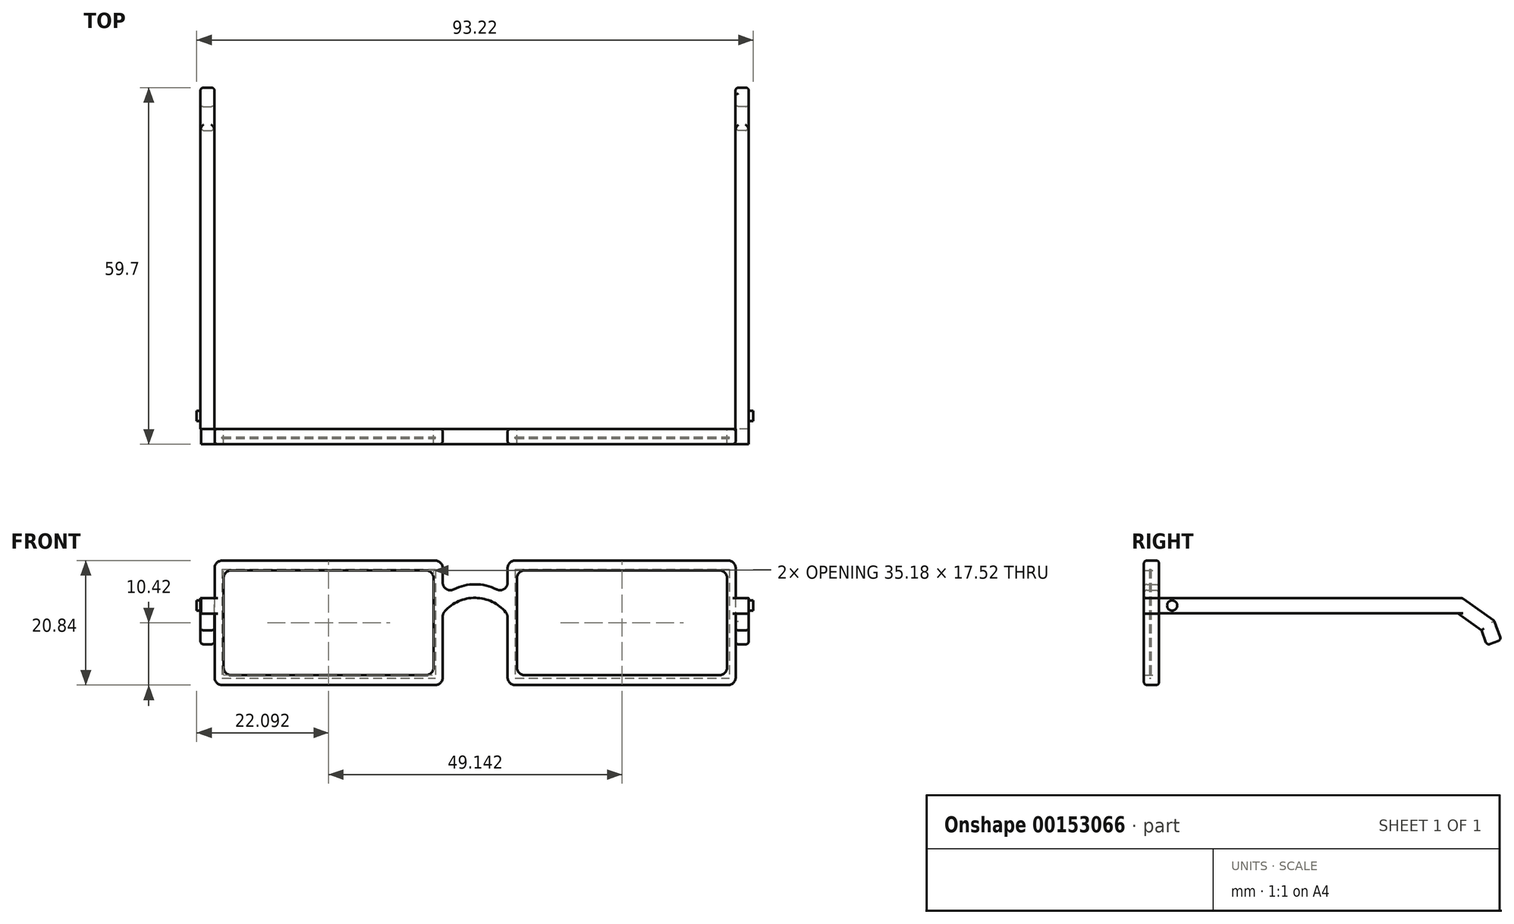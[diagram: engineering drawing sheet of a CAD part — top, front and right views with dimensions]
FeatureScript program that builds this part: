
annotation { "Feature Type Name" : "Feature", "Feature Type Description" : "" }
export const myFeature = defineFeature(function(context is Context, id is Id, definition is map)
    precondition{}
    {
        {
            var Q0;
            Q0=qCreatedBy(makeId("Front.planeOp"),FACE);
            var sketch = newSketch(context, id + "F0", { "sketchPlane" : qUnion([Q0])});
            skLineSegment(sketch, "E0", {"start": v(-49.06, 20.84) * mm, "end": v(-49.06, 0) * mm});
            skLineSegment(sketch, "E1", {"start": v(-49.06, 0) * mm, "end": v(-10.85, 0) * mm});
            skLineSegment(sketch, "E2", {"start": v(-10.85, 20.84) * mm, "end": v(-49.06, 20.84) * mm});
            skArc(sketch, "E3", {"start": v(0, 14.74) * mm, "mid": v(-5.43, 16.86) * mm, "end": v(-10.85, 14.74) * mm});
            skLineSegment(sketch, "E4", {"start": v(-10.85, 20.84) * mm, "end": v(-10.85, 14.74) * mm});
            skArc(sketch, "E5", {"start": v(0, 11.78) * mm, "mid": v(-5.39, 14.6) * mm, "end": v(-10.85, 11.94) * mm});
            skLineSegment(sketch, "E6", {"start": v(-10.85, 11.94) * mm, "end": v(-10.85, 0) * mm});
            skLineSegment(sketch, "E7", {"start": v(0, 14.74) * mm, "end": v(0, 20.84) * mm});
            skLineSegment(sketch, "E8", {"start": v(0, 11.78) * mm, "end": v(0, 0) * mm});
            skLineSegment(sketch, "E9", {"start": v(0, 0) * mm, "end": v(38.2, 0) * mm});
            skLineSegment(sketch, "E10", {"start": v(38.2, 0) * mm, "end": v(38.2, 20.84) * mm});
            skLineSegment(sketch, "E11", {"start": v(38.2, 20.84) * mm, "end": v(0, 20.84) * mm});
            skLineSegment(sketch, "E12.bottom", {"start": v(-47.57, 19.18) * mm, "end": v(-12.39, 19.18) * mm});
            skLineSegment(sketch, "E12.top", {"start": v(-47.57, 1.66) * mm, "end": v(-12.39, 1.66) * mm});
            skLineSegment(sketch, "E12.left", {"start": v(-47.57, 19.18) * mm, "end": v(-47.57, 1.66) * mm});
            skLineSegment(sketch, "E12.right", {"start": v(-12.39, 19.18) * mm, "end": v(-12.39, 1.66) * mm});
            skLineSegment(sketch, "E13.bottom", {"start": v(1.58, 19.18) * mm, "end": v(36.75, 19.18) * mm});
            skLineSegment(sketch, "E13.top", {"start": v(1.58, 1.66) * mm, "end": v(36.75, 1.66) * mm});
            skLineSegment(sketch, "E13.left", {"start": v(1.58, 19.18) * mm, "end": v(1.58, 1.66) * mm});
            skLineSegment(sketch, "E13.right", {"start": v(36.75, 19.18) * mm, "end": v(36.75, 1.66) * mm});
            skSolve(sketch);
        }
        {
            var Q0;
            Q0 = qSketchRegion(id + "F0", true);
            extrude(context, id + "F1", {"entities" : qUnion([Q0]), "depth" : 2.54 * mm});
        }
        {
            var Q0;
            Q0=makeQuery(id+"F1.opExtrude","SWEPT_EDGE",EDGE,{"disambiguationData":[OSD([sQuery(id+"F0.wireOp",EDGE,"E0"),sQuery(id+"F0.wireOp",EDGE,"E2")])]});
            var Q1;
            Q1=makeQuery(id+"F1.opExtrude","SWEPT_EDGE",EDGE,{"disambiguationData":[OSD([sQuery(id+"F0.wireOp",EDGE,"E0"),sQuery(id+"F0.wireOp",EDGE,"E1")])]});
            var Q2;
            Q2=makeQuery(id+"F1.opExtrude","SWEPT_EDGE",EDGE,{"disambiguationData":[OSD([sQuery(id+"F0.wireOp",EDGE,"E2"),sQuery(id+"F0.wireOp",EDGE,"E4")])]});
            var Q3;
            Q3=makeQuery(id+"F1.opExtrude","SWEPT_EDGE",EDGE,{"disambiguationData":[OSD([sQuery(id+"F0.wireOp",EDGE,"E1"),sQuery(id+"F0.wireOp",EDGE,"E6")])]});
            var Q4;
            Q4=makeQuery(id+"F1.opExtrude","SWEPT_EDGE",EDGE,{"disambiguationData":[OSD([sQuery(id+"F0.wireOp",EDGE,"E12.bottom"),sQuery(id+"F0.wireOp",EDGE,"E12.right")])]});
            var Q5;
            Q5=makeQuery(id+"F1.opExtrude","SWEPT_EDGE",EDGE,{"disambiguationData":[OSD([sQuery(id+"F0.wireOp",EDGE,"E12.top"),sQuery(id+"F0.wireOp",EDGE,"E12.right")])]});
            var Q6;
            Q6=makeQuery(id+"F1.opExtrude","SWEPT_EDGE",EDGE,{"disambiguationData":[OSD([sQuery(id+"F0.wireOp",EDGE,"E12.top"),sQuery(id+"F0.wireOp",EDGE,"E12.left")])]});
            var Q7;
            Q7=makeQuery(id+"F1.opExtrude","SWEPT_EDGE",EDGE,{"disambiguationData":[OSD([sQuery(id+"F0.wireOp",EDGE,"E12.bottom"),sQuery(id+"F0.wireOp",EDGE,"E12.left")])]});
            var Q8;
            Q8=makeQuery(id+"F1.opExtrude","SWEPT_EDGE",EDGE,{"disambiguationData":[OSD([sQuery(id+"F0.wireOp",EDGE,"E5"),sQuery(id+"F0.wireOp",EDGE,"E8")])]});
            var Q9;
            Q9=makeQuery(id+"F1.opExtrude","SWEPT_EDGE",EDGE,{"disambiguationData":[OSD([sQuery(id+"F0.wireOp",EDGE,"E5"),sQuery(id+"F0.wireOp",EDGE,"E6")])]});
            var Q10;
            Q10=makeQuery(id+"F1.opExtrude","SWEPT_EDGE",EDGE,{"disambiguationData":[OSD([sQuery(id+"F0.wireOp",EDGE,"E3"),sQuery(id+"F0.wireOp",EDGE,"E4")])]});
            var Q11;
            Q11=makeQuery(id+"F1.opExtrude","SWEPT_EDGE",EDGE,{"disambiguationData":[OSD([sQuery(id+"F0.wireOp",EDGE,"E3"),sQuery(id+"F0.wireOp",EDGE,"E7")])]});
            var Q12;
            Q12=makeQuery(id+"F1.opExtrude","SWEPT_EDGE",EDGE,{"disambiguationData":[OSD([sQuery(id+"F0.wireOp",EDGE,"E7"),sQuery(id+"F0.wireOp",EDGE,"E11")])]});
            var Q13;
            Q13=makeQuery(id+"F1.opExtrude","SWEPT_EDGE",EDGE,{"disambiguationData":[OSD([sQuery(id+"F0.wireOp",EDGE,"E8"),sQuery(id+"F0.wireOp",EDGE,"E9")])]});
            var Q14;
            Q14=makeQuery(id+"F1.opExtrude","SWEPT_EDGE",EDGE,{"disambiguationData":[OSD([sQuery(id+"F0.wireOp",EDGE,"E9"),sQuery(id+"F0.wireOp",EDGE,"E10")])]});
            var Q15;
            Q15=makeQuery(id+"F1.opExtrude","SWEPT_EDGE",EDGE,{"disambiguationData":[OSD([sQuery(id+"F0.wireOp",EDGE,"E10"),sQuery(id+"F0.wireOp",EDGE,"E11")])]});
            var Q16;
            Q16=makeQuery(id+"F1.opExtrude","SWEPT_EDGE",EDGE,{"disambiguationData":[OSD([sQuery(id+"F0.wireOp",EDGE,"E13.top"),sQuery(id+"F0.wireOp",EDGE,"E13.left")])]});
            var Q17;
            Q17=makeQuery(id+"F1.opExtrude","SWEPT_EDGE",EDGE,{"disambiguationData":[OSD([sQuery(id+"F0.wireOp",EDGE,"E13.bottom"),sQuery(id+"F0.wireOp",EDGE,"E13.left")])]});
            var Q18;
            Q18=makeQuery(id+"F1.opExtrude","SWEPT_EDGE",EDGE,{"disambiguationData":[OSD([sQuery(id+"F0.wireOp",EDGE,"E13.bottom"),sQuery(id+"F0.wireOp",EDGE,"E13.right")])]});
            var Q19;
            Q19=makeQuery(id+"F1.opExtrude","SWEPT_EDGE",EDGE,{"disambiguationData":[OSD([sQuery(id+"F0.wireOp",EDGE,"E13.top"),sQuery(id+"F0.wireOp",EDGE,"E13.right")])]});
            fillet(context, id + "F2", {"entities" : qUnion([Q0, Q1, Q2, Q3, Q4, Q5, Q6, Q7, Q8, Q9, Q10, Q11, Q12, Q13, Q14, Q15, Q16, Q17, Q18, Q19]), "radius" : 1.27 * mm, "tangentPropagation" : true, "allowEdgeOverflow" : false});
        }
        {
            var Q0;
            Q0=makeQuery(id+"F1.opExtrude","SWEPT_FACE",FACE,{"disambiguationData":[OSD([sQuery(id+"F0.wireOp",EDGE,"E10")])]});
            var sketch = newSketch(context, id + "F3", { "sketchPlane" : qUnion([Q0])});
            skLineSegment(sketch, "E14.bottom", {"start": v(-2.54, 14.53) * mm, "end": v(0, 14.53) * mm});
            skLineSegment(sketch, "E14.top", {"start": v(-2.54, 11.93) * mm, "end": v(0, 11.93) * mm});
            skLineSegment(sketch, "E14.left", {"start": v(-2.54, 14.53) * mm, "end": v(-2.54, 11.93) * mm});
            skLineSegment(sketch, "E14.right", {"start": v(0, 14.53) * mm, "end": v(0, 11.93) * mm});
            skLineSegment(sketch, "E15.bottom", {"start": v(0, 14.53) * mm, "end": v(-2.54, 14.53) * mm});
            skLineSegment(sketch, "E15.top", {"start": v(0, 11.93) * mm, "end": v(-2.54, 11.93) * mm});
            skSolve(sketch);
        }
        {
            var Q0;
            Q0 = qSketchRegion(id + "F3", true);
            extrude(context, id + "F4", {"entities" : qUnion([Q0]), "operationType" : NewBodyOperationType.ADD, "depth" : 2.16 * mm});
        }
        {
            var Q0;
            Q0 = qSketchRegion(id + "F3", true);
            extrude(context, id + "F5", {"entities" : qUnion([Q0]), "operationType" : NewBodyOperationType.ADD, "oppositeDirection" : true, "depth" : 89.53 * mm, "hasSecondDirection" : true, "secondDirectionOppositeDirection" : true, "secondDirectionDepth" : 87 * mm});
        }
        {
            var Q0;
            Q0=qCreatedBy(makeId("Right.planeOp"),FACE);
            var sketch = newSketch(context, id + "F6", { "sketchPlane" : qUnion([Q0])});
            skLineSegment(sketch, "E16", {"start": v(0, 14.54) * mm, "end": v(50.8, 14.54) * mm});
            skLineSegment(sketch, "E17", {"start": v(50.8, 14.54) * mm, "end": v(56.1, 10.78) * mm});
            skLineSegment(sketch, "E18", {"start": v(56.1, 10.78) * mm, "end": v(57.3, 7.55) * mm});
            skLineSegment(sketch, "E19.0", {"start": v(54, 9.16) * mm, "end": v(54.91, 6.67) * mm});
            skLineSegment(sketch, "E19.1", {"start": v(50, 12) * mm, "end": v(54, 9.16) * mm});
            skLineSegment(sketch, "E19.2", {"start": v(0, 12) * mm, "end": v(50, 12) * mm});
            skLineSegment(sketch, "E20", {"start": v(57.3, 7.55) * mm, "end": v(54.91, 6.67) * mm});
            skLineSegment(sketch, "E21", {"start": v(0, 14.54) * mm, "end": v(0, 12) * mm});
            skSolve(sketch);
        }
        {
            var Q0;
            Q0 = qSketchRegion(id + "F6", true);
            extrude(context, id + "F7", {"entities" : qUnion([Q0]), "operationType" : NewBodyOperationType.ADD, "depth" : 40.4 * mm, "hasSecondDirection" : true, "secondDirectionOppositeDirection" : false, "secondDirectionDepth" : 38.16 * mm});
        }
        {
            var Q0;
            Q0=qCreatedBy(makeId("Right.planeOp"),FACE);
            var sketch = newSketch(context, id + "F8", { "sketchPlane" : qUnion([Q0])});
            skLineSegment(sketch, "E22", {"start": v(0, 14.54) * mm, "end": v(50.8, 14.54) * mm});
            skLineSegment(sketch, "E23", {"start": v(50.8, 14.54) * mm, "end": v(56.1, 10.79) * mm});
            skLineSegment(sketch, "E24", {"start": v(56.1, 10.79) * mm, "end": v(57.3, 7.58) * mm});
            skLineSegment(sketch, "E25", {"start": v(57.3, 7.58) * mm, "end": v(54.93, 6.68) * mm});
            skLineSegment(sketch, "E26", {"start": v(54.93, 6.68) * mm, "end": v(53.99, 9.17) * mm});
            skLineSegment(sketch, "E27", {"start": v(53.99, 9.17) * mm, "end": v(50, 12) * mm});
            skLineSegment(sketch, "E28", {"start": v(50, 12) * mm, "end": v(0, 12) * mm});
            skLineSegment(sketch, "E29", {"start": v(0, 12) * mm, "end": v(0, 14.54) * mm});
            skSolve(sketch);
        }
        {
            var Q0;
            Q0 = qSketchRegion(id + "F8", true);
            extrude(context, id + "F9", {"entities" : qUnion([Q0]), "operationType" : NewBodyOperationType.ADD, "oppositeDirection" : true, "depth" : 51.43 * mm, "hasSecondDirection" : true, "secondDirectionOppositeDirection" : true, "secondDirectionDepth" : 49.1 * mm});
        }
        {
            var Q0;
            Q0=makeQuery(id+"F9.opExtrude","CAP_EDGE",EDGE,{"disambiguationData":[OSD([sQuery(id+"F8.wireOp",EDGE,"E27")])],"isStart":false});
            var Q1;
            Q1=makeQuery(id+"F9.opExtrude","CAP_EDGE",EDGE,{"disambiguationData":[OSD([sQuery(id+"F8.wireOp",EDGE,"E26")])],"isStart":false});
            var Q2;
            Q2=makeQuery(id+"F9.opExtrude","CAP_EDGE",EDGE,{"disambiguationData":[OSD([sQuery(id+"F8.wireOp",EDGE,"E27")])],"isStart":true});
            var Q3;
            Q3=makeQuery(id+"F9.opExtrude","CAP_EDGE",EDGE,{"disambiguationData":[OSD([sQuery(id+"F8.wireOp",EDGE,"E26")])],"isStart":true});
            var Q4;
            Q4=makeQuery(id+"F9.opExtrude","CAP_EDGE",EDGE,{"disambiguationData":[OSD([sQuery(id+"F8.wireOp",EDGE,"E25")])],"isStart":false});
            var Q5;
            Q5=makeQuery(id+"F9.opExtrude","SWEPT_EDGE",EDGE,{"disambiguationData":[OSD([sQuery(id+"F8.wireOp",EDGE,"E24"),sQuery(id+"F8.wireOp",EDGE,"E25")])]});
            var Q6;
            Q6=makeQuery(id+"F9.opExtrude","CAP_EDGE",EDGE,{"disambiguationData":[OSD([sQuery(id+"F8.wireOp",EDGE,"E25")])],"isStart":true});
            var Q7;
            Q7=makeQuery(id+"F9.opExtrude","SWEPT_EDGE",EDGE,{"disambiguationData":[OSD([sQuery(id+"F8.wireOp",EDGE,"E25"),sQuery(id+"F8.wireOp",EDGE,"E26")])]});
            var Q8;
            Q8=makeQuery(id+"F9.opExtrude","SWEPT_EDGE",EDGE,{"disambiguationData":[OSD([sQuery(id+"F8.wireOp",EDGE,"E23"),sQuery(id+"F8.wireOp",EDGE,"E24")])]});
            var Q9;
            Q9=makeQuery(id+"F9.opExtrude","SWEPT_EDGE",EDGE,{"disambiguationData":[OSD([sQuery(id+"F8.wireOp",EDGE,"E22"),sQuery(id+"F8.wireOp",EDGE,"E23")])]});
            var Q10;
            Q10=makeQuery(id+"F9.opExtrude","CAP_EDGE",EDGE,{"disambiguationData":[OSD([sQuery(id+"F8.wireOp",EDGE,"E24")])],"isStart":false});
            var Q11;
            Q11=makeQuery(id+"F9.opExtrude","CAP_EDGE",EDGE,{"disambiguationData":[OSD([sQuery(id+"F8.wireOp",EDGE,"E23")])],"isStart":false});
            var Q12;
            Q12=makeQuery(id+"F9.opExtrude","CAP_EDGE",EDGE,{"disambiguationData":[OSD([sQuery(id+"F8.wireOp",EDGE,"E24")])],"isStart":true});
            var Q13;
            Q13=makeQuery(id+"F9.opExtrude","CAP_EDGE",EDGE,{"disambiguationData":[OSD([sQuery(id+"F8.wireOp",EDGE,"E23")])],"isStart":true});
            fillet(context, id + "F10", {"entities" : qUnion([Q0, Q1, Q2, Q3, Q4, Q5, Q6, Q7, Q8, Q9, Q10, Q11, Q12, Q13]), "radius" : 0.5 * mm, "tangentPropagation" : true, "allowEdgeOverflow" : false});
        }
        {
            var Q0;
            Q0=makeQuery(id+"F7.opExtrude","CAP_EDGE",EDGE,{"disambiguationData":[OSD([sQuery(id+"F6.wireOp",EDGE,"E18")])],"isStart":true});
            var Q1;
            Q1=makeQuery(id+"F7.opExtrude","CAP_EDGE",EDGE,{"disambiguationData":[OSD([sQuery(id+"F6.wireOp",EDGE,"E17")])],"isStart":true});
            var Q2;
            Q2=makeQuery(id+"F7.opExtrude","CAP_EDGE",EDGE,{"disambiguationData":[OSD([sQuery(id+"F6.wireOp",EDGE,"E19.1")])],"isStart":true});
            var Q3;
            Q3=makeQuery(id+"F7.opExtrude","CAP_EDGE",EDGE,{"disambiguationData":[OSD([sQuery(id+"F6.wireOp",EDGE,"E19.0")])],"isStart":true});
            var Q4;
            Q4=makeQuery(id+"F7.opExtrude","CAP_EDGE",EDGE,{"disambiguationData":[OSD([sQuery(id+"F6.wireOp",EDGE,"E20")])],"isStart":true});
            var Q5;
            Q5=makeQuery(id+"F7.opExtrude","SWEPT_EDGE",EDGE,{"disambiguationData":[OSD([sQuery(id+"F6.wireOp",EDGE,"E19.0"),sQuery(id+"F6.wireOp",EDGE,"E20")])]});
            var Q6;
            Q6=makeQuery(id+"F7.opExtrude","CAP_EDGE",EDGE,{"disambiguationData":[OSD([sQuery(id+"F6.wireOp",EDGE,"E20")])],"isStart":false});
            var Q7;
            Q7=makeQuery(id+"F7.opExtrude","SWEPT_EDGE",EDGE,{"disambiguationData":[OSD([sQuery(id+"F6.wireOp",EDGE,"E18"),sQuery(id+"F6.wireOp",EDGE,"E20")])]});
            var Q8;
            Q8=makeQuery(id+"F7.opExtrude","CAP_EDGE",EDGE,{"disambiguationData":[OSD([sQuery(id+"F6.wireOp",EDGE,"E18")])],"isStart":false});
            var Q9;
            Q9=makeQuery(id+"F7.opExtrude","CAP_EDGE",EDGE,{"disambiguationData":[OSD([sQuery(id+"F6.wireOp",EDGE,"E19.1")])],"isStart":false});
            var Q10;
            Q10=makeQuery(id+"F7.opExtrude","CAP_EDGE",EDGE,{"disambiguationData":[OSD([sQuery(id+"F6.wireOp",EDGE,"E19.0")])],"isStart":false});
            var Q11;
            Q11=makeQuery(id+"F7.opExtrude","CAP_EDGE",EDGE,{"disambiguationData":[OSD([sQuery(id+"F6.wireOp",EDGE,"E17")])],"isStart":false});
            var Q12;
            Q12=makeQuery(id+"F7.opExtrude","SWEPT_EDGE",EDGE,{"disambiguationData":[OSD([sQuery(id+"F6.wireOp",EDGE,"E17"),sQuery(id+"F6.wireOp",EDGE,"E18")])]});
            var Q13;
            Q13=makeQuery(id+"F7.opExtrude","SWEPT_EDGE",EDGE,{"disambiguationData":[OSD([sQuery(id+"F6.wireOp",EDGE,"E16"),sQuery(id+"F6.wireOp",EDGE,"E17")])]});
            fillet(context, id + "F11", {"entities" : qUnion([Q0, Q1, Q2, Q3, Q4, Q5, Q6, Q7, Q8, Q9, Q10, Q11, Q12, Q13]), "radius" : 0.5 * mm, "tangentPropagation" : true, "allowEdgeOverflow" : false});
        }
        {
            var Q0;
            Q0=makeQuery(id+"F1.opExtrude","CAP_EDGE",EDGE,{"disambiguationData":[OSD([sQuery(id+"F0.wireOp",EDGE,"E5")])],"isStart":false});
            var Q1;
            Q1=makeQuery(id+"F1.opExtrude","CAP_EDGE",EDGE,{"disambiguationData":[OSD([sQuery(id+"F0.wireOp",EDGE,"E3")])],"isStart":false});
            var Q2;
            Q2=makeQuery(id+"F1.opExtrude","CAP_EDGE",EDGE,{"disambiguationData":[OSD([sQuery(id+"F0.wireOp",EDGE,"E3")])],"isStart":true});
            var Q3;
            Q3=makeQuery(id+"F1.opExtrude","CAP_EDGE",EDGE,{"disambiguationData":[OSD([sQuery(id+"F0.wireOp",EDGE,"E5")])],"isStart":true});
            fillet(context, id + "F12", {"entities" : qUnion([Q0, Q1, Q2, Q3]), "radius" : 0.5 * mm, "tangentPropagation" : true, "allowEdgeOverflow" : false});
        }
        {
            var Q0;
            Q0=qCreatedBy(makeId("Right.planeOp"),FACE);
            var sketch = newSketch(context, id + "F13", { "sketchPlane" : qUnion([Q0])});
            skCircle(sketch, "E30", {"center": v(2.18, 13.31) * mm, "radius": 0.85 * mm});
            skSolve(sketch);
        }
        {
            var Q0;
            Q0 = qSketchRegion(id + "F13", true);
            extrude(context, id + "F14", {"entities" : qUnion([Q0]), "operationType" : NewBodyOperationType.ADD, "oppositeDirection" : true, "depth" : 52.07 * mm, "hasSecondDirection" : true, "secondDirectionOppositeDirection" : true, "secondDirectionDepth" : 50.04 * mm});
        }
        {
            var Q0;
            Q0=qCreatedBy(makeId("Front.planeOp"),FACE);
            var sketch = newSketch(context, id + "F15", { "sketchPlane" : qUnion([Q0])});
            skLineSegment(sketch, "E31.bottom", {"start": v(-47.8, 19.35) * mm, "end": v(-12.05, 19.35) * mm});
            skLineSegment(sketch, "E31.top", {"start": v(-47.8, 1.16) * mm, "end": v(-12.05, 1.16) * mm});
            skLineSegment(sketch, "E31.left", {"start": v(-47.8, 19.35) * mm, "end": v(-47.8, 1.16) * mm});
            skLineSegment(sketch, "E31.right", {"start": v(-12.05, 19.35) * mm, "end": v(-12.05, 1.16) * mm});
            skLineSegment(sketch, "E32.bottom", {"start": v(1.27, 19.4) * mm, "end": v(37.13, 19.4) * mm});
            skLineSegment(sketch, "E32.top", {"start": v(1.27, 1.16) * mm, "end": v(37.13, 1.16) * mm});
            skLineSegment(sketch, "E32.left", {"start": v(1.27, 19.4) * mm, "end": v(1.27, 1.16) * mm});
            skLineSegment(sketch, "E32.right", {"start": v(37.13, 19.4) * mm, "end": v(37.13, 1.16) * mm});
            skSolve(sketch);
        }
        {
            var Q0;
            Q0 = qSketchRegion(id + "F15", true);
            extrude(context, id + "F16", {"entities" : qUnion([Q0]), "depth" : 1.59 * mm, "hasSecondDirection" : true, "secondDirectionOppositeDirection" : false, "secondDirectionDepth" : 1.33 * mm});
        }
        {
            var Q0;
            Q0 = qSketchRegion(id + "F13", true);
            extrude(context, id + "F17", {"entities" : qUnion([Q0]), "operationType" : NewBodyOperationType.ADD, "depth" : 41.15 * mm, "hasSecondDirection" : true, "secondDirectionOppositeDirection" : false, "secondDirectionDepth" : 39.24 * mm});
        }
    });
